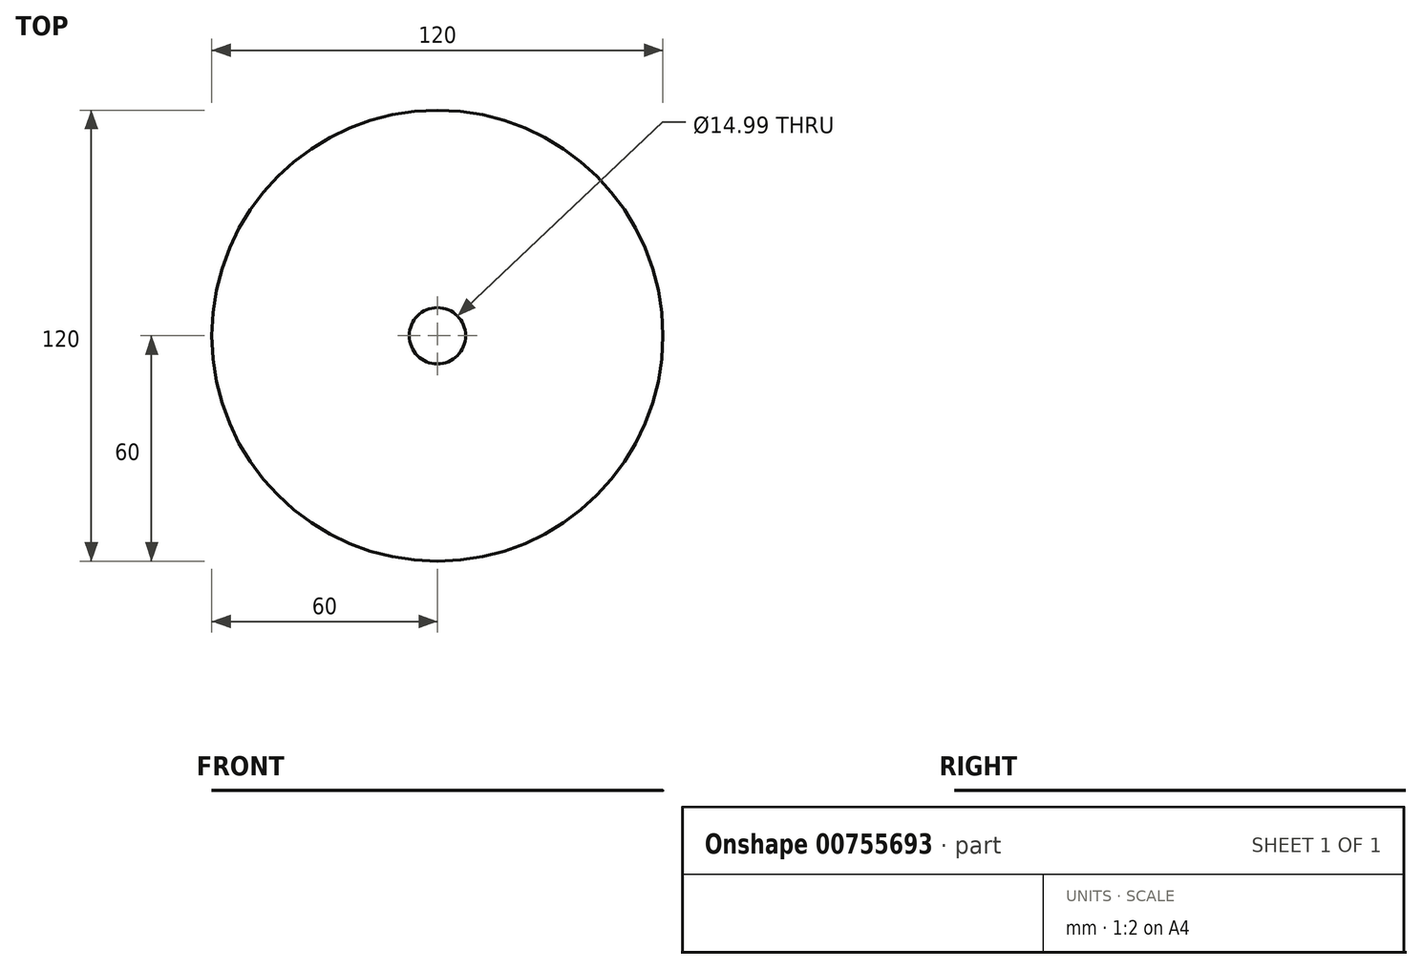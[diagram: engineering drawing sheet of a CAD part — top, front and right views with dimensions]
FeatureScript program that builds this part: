
annotation { "Feature Type Name" : "Feature", "Feature Type Description" : "" }
export const myFeature = defineFeature(function(context is Context, id is Id, definition is map)
    precondition{}
    {
        {
            var Q0;
            Q0=qCreatedBy(makeId("Top.planeOp"),FACE);
            var sketch = newSketch(context, id + "F0", { "sketchPlane" : qUnion([Q0])});
            skCircle(sketch, "E0", {"center": v(0, 0) * mm, "radius": 60 * mm});
            skCircle(sketch, "E1", {"center": v(0, 0) * mm, "radius": 7.5 * mm});
            skSolve(sketch);
        }
        {
            var Q0;
            Q0 = qSketchRegion(id + "F0", true);
            extrude(context, id + "F1", {"entities" : qUnion([Q0]), "depth" : 1 / 203.2 * mm, "offsetDistance" : 25.4 * mm});
        }
    });
